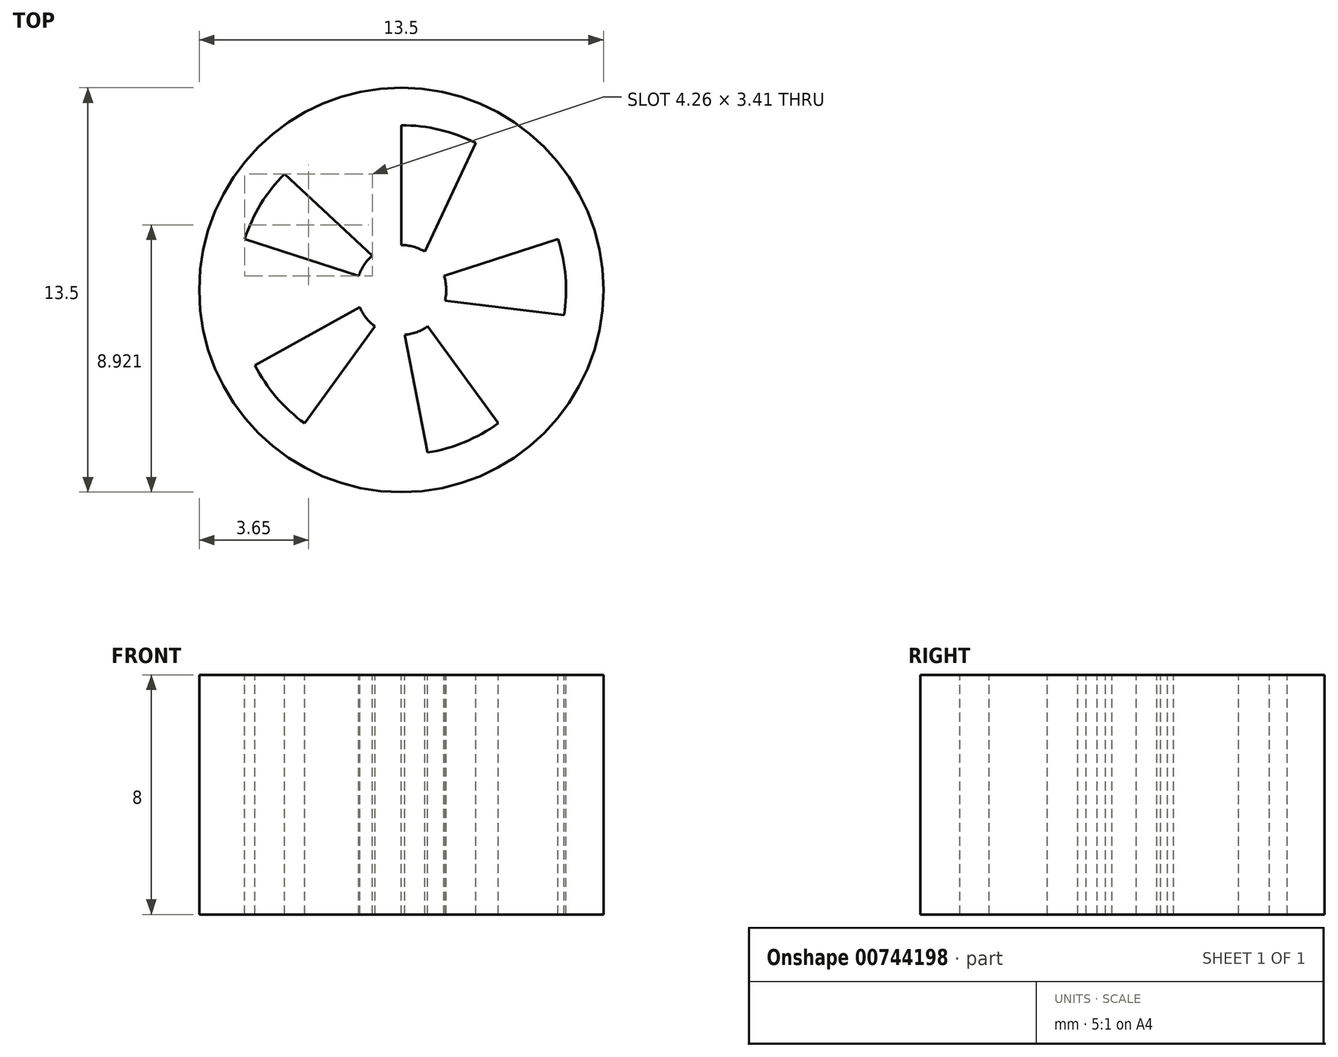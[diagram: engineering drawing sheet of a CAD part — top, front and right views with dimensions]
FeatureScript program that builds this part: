
annotation { "Feature Type Name" : "Feature", "Feature Type Description" : "" }
export const myFeature = defineFeature(function(context is Context, id is Id, definition is map)
    precondition{}
    {
        {
            var Q0;
            Q0=qCreatedBy(makeId("Top.planeOp"),FACE);
            var sketch = newSketch(context, id + "F0", { "sketchPlane" : qUnion([Q0])});
            skCircle(sketch, "E0", {"center": v(0, 0) * mm, "radius": 6.75 * mm});
            skSolve(sketch);
        }
        {
            var Q0;
            Q0 = qSketchRegion(id + "F0", true);
            extrude(context, id + "F1", {"entities" : qUnion([Q0]), "depth" : 8 * mm, "offsetDistance" : 25 * mm});
        }
        {
            var Q0;
            Q0=makeQuery(id+"F1.opExtrude","CAP_FACE",FACE,{"disambiguationData":[OSD([sQuery(id+"F0.wireOp",EDGE,"E0")])],"isStart":false});
            var sketch = newSketch(context, id + "F2", { "sketchPlane" : qUnion([Q0])});
            skCircle(sketch, "E1", {"center": v(0, 0) * mm, "radius": 1.5 * mm});
            skCircle(sketch, "E2", {"center": v(0, 0) * mm, "radius": 5.5 * mm});
            skLineSegment(sketch, "E3", {"start": v(0, 1.5) * mm, "end": v(0, 5.5) * mm});
            skLineSegment(sketch, "E4", {"start": v(0.79, 1.28) * mm, "end": v(2.48, 4.9) * mm});
            skLineSegment(sketch, "E5.1.0", {"start": v(-1.43, 0.46) * mm, "end": v(-5.23, 1.7) * mm});
            skLineSegment(sketch, "E5.1.1", {"start": v(-0.97, 1.14) * mm, "end": v(-3.9, 3.88) * mm});
            skLineSegment(sketch, "E5.2.0", {"start": v(-0.88, -1.21) * mm, "end": v(-3.23, -4.45) * mm});
            skLineSegment(sketch, "E5.2.1", {"start": v(-1.39, -0.57) * mm, "end": v(-4.9, -2.51) * mm});
            skLineSegment(sketch, "E5.3.0", {"start": v(0.88, -1.21) * mm, "end": v(3.23, -4.45) * mm});
            skLineSegment(sketch, "E5.3.1", {"start": v(0.11, -1.5) * mm, "end": v(0.88, -5.43) * mm});
            skLineSegment(sketch, "E5.4.0", {"start": v(1.43, 0.46) * mm, "end": v(5.23, 1.7) * mm});
            skLineSegment(sketch, "E5.4.1", {"start": v(1.46, -0.36) * mm, "end": v(5.43, -0.84) * mm});
            skSolve(sketch);
        }
        {
            var Q0;
            {var subQ0=sQuery(id+"F2.wireOp",EDGE,"E3");Q0=makeQuery(id+"F2.imprint","IMPRINT",FACE,{"disambiguationData":[TD([[makeQuery(id+"F2.imprint","IMPRINT",EDGE,{"derivedFrom":subQ0}),-1.0]])]});}
            var Q1;
            {var subQ0=sQuery(id+"F2.wireOp",EDGE,"E5.1.0");Q1=makeQuery(id+"F2.imprint","IMPRINT",FACE,{"disambiguationData":[TD([[makeQuery(id+"F2.imprint","IMPRINT",EDGE,{"derivedFrom":subQ0}),-1.0]])]});}
            var Q2;
            {var subQ0=sQuery(id+"F2.wireOp",EDGE,"E5.2.0");Q2=makeQuery(id+"F2.imprint","IMPRINT",FACE,{"disambiguationData":[TD([[makeQuery(id+"F2.imprint","IMPRINT",EDGE,{"derivedFrom":subQ0}),-1.0]])]});}
            var Q3;
            {var subQ0=sQuery(id+"F2.wireOp",EDGE,"E5.3.0");Q3=makeQuery(id+"F2.imprint","IMPRINT",FACE,{"disambiguationData":[TD([[makeQuery(id+"F2.imprint","IMPRINT",EDGE,{"derivedFrom":subQ0}),-1.0]])]});}
            var Q4;
            {var subQ0=sQuery(id+"F2.wireOp",EDGE,"E5.4.0");Q4=makeQuery(id+"F2.imprint","IMPRINT",FACE,{"disambiguationData":[TD([[makeQuery(id+"F2.imprint","IMPRINT",EDGE,{"derivedFrom":subQ0}),-1.0]])]});}
            extrude(context, id + "F3", {"entities" : qUnion([Q0, Q1, Q2, Q3, Q4]), "operationType" : NewBodyOperationType.REMOVE, "endBound" : BoundingType.THROUGH_ALL, "oppositeDirection" : true, "depth" : 25 * mm, "offsetDistance" : 25 * mm});
        }
    });
